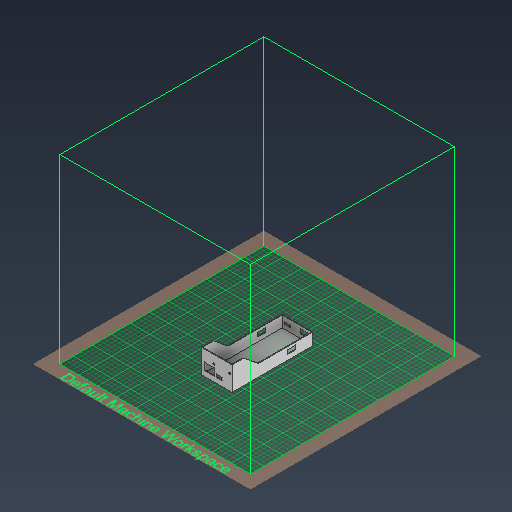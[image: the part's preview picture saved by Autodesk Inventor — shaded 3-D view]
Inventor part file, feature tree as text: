
AUTODESK INVENTOR PART (.ipt)
format: ipt  version: 2021 (Build 250183000, 183)  size: 389,632 bytes
history: native  units: in
note: dims shown in document units (in); Inventor stores cm internally (conversion verified against a paired STEP export)
features: extrude x8, sketch x8, shell x1
ambient origin geometry x8: Origin, YZ Plane, XZ Plane, XY Plane, X Axis, Y Axis, Z Axis, Center Point
bodies: Solid1 (feature_tree)
feature tree (17):
  extrude  "Extrusion1"  Depth=6.9in
  shell  "Shell1"  Thickness=2.0in
  sketch  "Sketch2"  dims[d4=0.0625in d5=0.375in]
  sketch  "Sketch4"  dims[d6=2.55in d7=0.1875in]
  extrude  "Extrusion2"  Depth=0.375in
  extrude  "Extrusion3"  Depth=0.1875in
  extrude  "Extrusion4"  Depth=0.72in
  extrude  "Extrusion5"  Depth=1.0in
  extrude  "Extrusion6"  Depth=0.375in
  extrude  "Extrusion7"  Depth=0.875in
  extrude  "Extrusion8"  Depth=1.0625in
  sketch  "Sketch1"  dims[d0=2.55in d1=6.9in d2=2.0in d3=0.0in]
  sketch  "Sketch5"  dims[d8=0.56in d9=0.72in]
  sketch  "Sketch6"  dims[d10=0.75in d11=1.0in]
  sketch  "Sketch7"  dims[d12=0.35in d13=0.375in]
  sketch  "Sketch8"  dims[d14=2.55in d15=0.875in]
  sketch  "Sketch9"  dims[d16=0.625in d17=1.0625in d18=0.5in d19=0.25in d20=1.3125in d21=0.375in d22=6.9in d23=0.7in d24=0.35in d25=2.12in d26=6.75in d27=0.0in d28=6.75in d29=0.0in d30=6.75in d31=0.0in d32=1.0in d33=6.75in d34=0.0in d35=0.1772in d36=0.205in d37=0.728in d38=0.1772in d39=1.378in d40=6.75in d41=0.0in d42=0.4331in d43=0.315in d44=0.689in d45=0.3937in d46=0.0in d47=0.1181in d48=0.1181in d49=1.1614in d50=0.1969in d51=0.5906in d52=0.5906in d53=0.3937in d54=0.0in]
